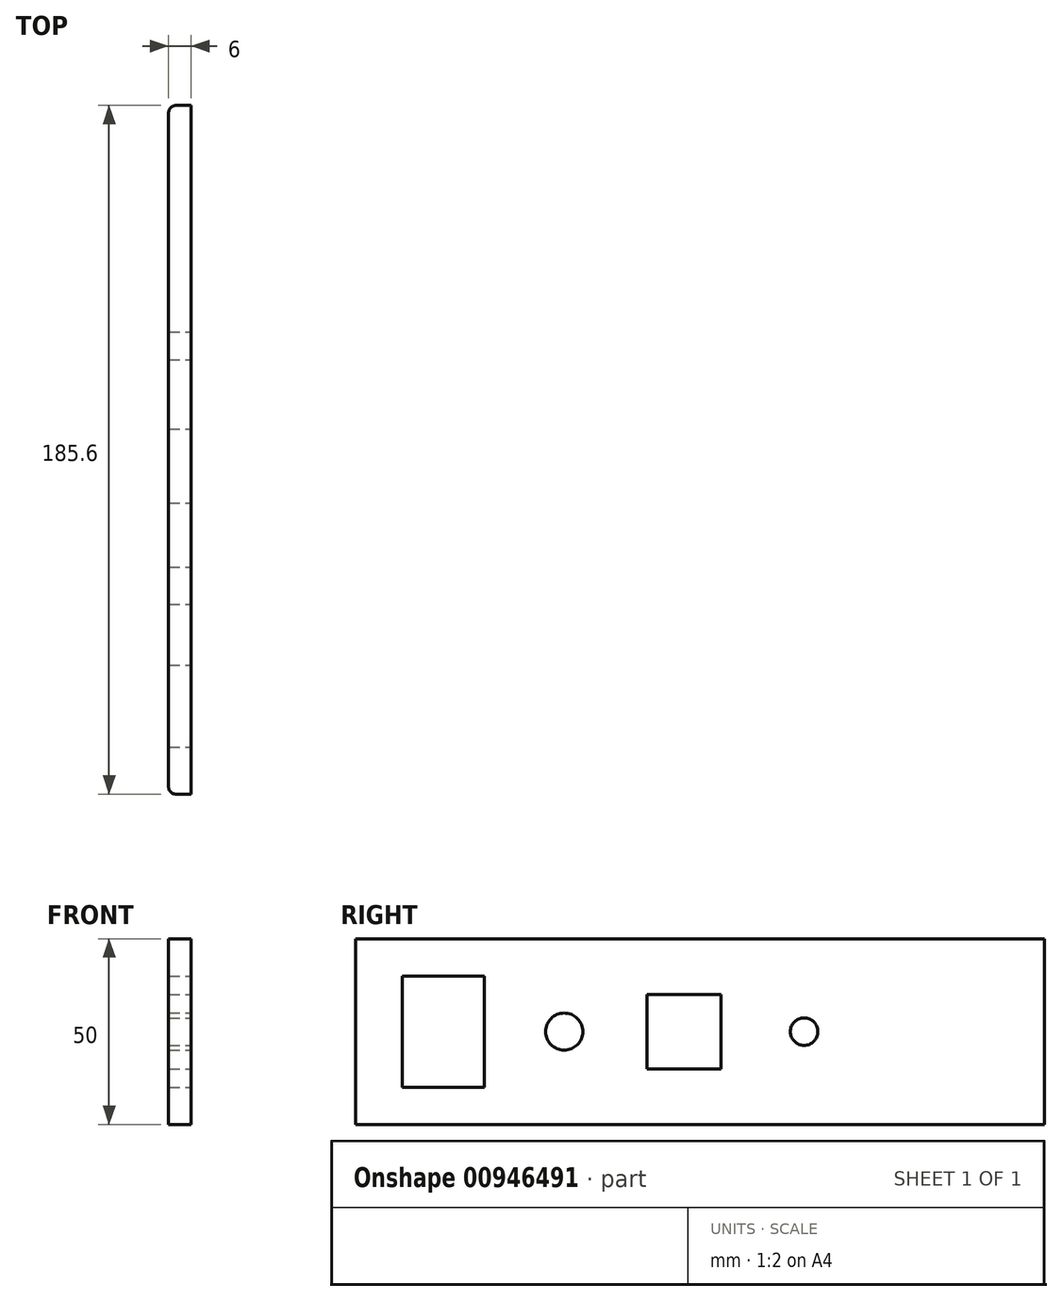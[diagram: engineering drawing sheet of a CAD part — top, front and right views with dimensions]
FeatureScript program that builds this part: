
annotation { "Feature Type Name" : "Feature", "Feature Type Description" : "" }
export const myFeature = defineFeature(function(context is Context, id is Id, definition is map)
    precondition{}
    {
        {
            var Q0;
            Q0=qCreatedBy(makeId("Right.planeOp"),FACE);
            var sketch = newSketch(context, id + "F0", { "sketchPlane" : qUnion([Q0])});
            skLineSegment(sketch, "E0.bottom", {"start": v(92.8, 25) * mm, "end": v(-92.8, 25) * mm});
            skLineSegment(sketch, "E0.top", {"start": v(92.8, -25) * mm, "end": v(-92.8, -25) * mm});
            skLineSegment(sketch, "E0.left", {"start": v(92.8, 25) * mm, "end": v(92.8, -25) * mm});
            skLineSegment(sketch, "E0.right", {"start": v(-92.8, 25) * mm, "end": v(-92.8, -25) * mm});
            skPoint(sketch, "E0.middle", {"position": v(0, 0) * mm});
            skSolve(sketch);
        }
        {
            var Q0;
            Q0=makeQuery(id+"F0.imprint","IMPRINT",FACE,{"disambiguationData":[TD([[makeQuery(id+"F0.imprint","IMPRINT",EDGE,{"derivedFrom":sQuery(id+"F0.wireOp",EDGE,"E0.bottom")}),1.0]])]});
            extrude(context, id + "F1", {"entities" : qUnion([Q0]), "depth" : 6 * mm, "offsetDistance" : 25 * mm});
        }
        {
            var Q0;
            Q0=makeQuery(id+"F1.opExtrude","CAP_FACE",FACE,{"disambiguationData":[OSD([sQuery(id+"F0.wireOp",EDGE,"E0.bottom"),sQuery(id+"F0.wireOp",EDGE,"E0.top"),sQuery(id+"F0.wireOp",EDGE,"E0.left"),sQuery(id+"F0.wireOp",EDGE,"E0.right")])],"isStart":false});
            var sketch = newSketch(context, id + "F2", { "sketchPlane" : qUnion([Q0])});
            skLineSegment(sketch, "E1.bottom", {"start": v(-58.05, -15) * mm, "end": v(-80.15, -15) * mm});
            skLineSegment(sketch, "E1.top", {"start": v(-58.05, 15) * mm, "end": v(-80.15, 15) * mm});
            skLineSegment(sketch, "E1.left", {"start": v(-58.05, -15) * mm, "end": v(-58.05, 15) * mm});
            skLineSegment(sketch, "E1.right", {"start": v(-80.15, -15) * mm, "end": v(-80.15, 15) * mm});
            skPoint(sketch, "E1.middle", {"position": v(-69.1, 0) * mm});
            skSolve(sketch);
        }
        {
            var Q0;
            Q0=makeQuery(id+"F2.imprint","IMPRINT",FACE,{"disambiguationData":[TD([[makeQuery(id+"F2.imprint","IMPRINT",EDGE,{"derivedFrom":sQuery(id+"F2.wireOp",EDGE,"E1.bottom")}),-1.0]])]});
            extrude(context, id + "F3", {"entities" : qUnion([Q0]), "operationType" : NewBodyOperationType.REMOVE, "endBound" : BoundingType.UP_TO_NEXT, "oppositeDirection" : true, "depth" : 25 * mm, "offsetDistance" : 25 * mm});
        }
        {
            var Q0;
            Q0=makeQuery(id+"F1.opExtrude","CAP_FACE",FACE,{"disambiguationData":[OSD([sQuery(id+"F0.wireOp",EDGE,"E0.bottom"),sQuery(id+"F0.wireOp",EDGE,"E0.top"),sQuery(id+"F0.wireOp",EDGE,"E0.left"),sQuery(id+"F0.wireOp",EDGE,"E0.right")])],"isStart":false});
            var sketch = newSketch(context, id + "F4", { "sketchPlane" : qUnion([Q0])});
            skCircle(sketch, "E2", {"center": v(-36.6, 0) * mm, "radius": 5 * mm});
            skSolve(sketch);
        }
        {
            var Q0;
            Q0=makeQuery(id+"F4.imprint","IMPRINT",FACE,{"disambiguationData":[TD([[makeQuery(id+"F4.imprint","IMPRINT",EDGE,{"derivedFrom":sQuery(id+"F4.wireOp",EDGE,"E2")}),1.0]])]});
            var Q1;
            Q1=sQuery(id+"F4.wireOp",EDGE,"E2");
            extrude(context, id + "F5", {"entities" : qUnion([Q0]), "operationType" : NewBodyOperationType.REMOVE, "surfaceEntities" : qUnion([Q1]), "endBound" : BoundingType.UP_TO_NEXT, "oppositeDirection" : true, "depth" : 25 * mm, "offsetDistance" : 25 * mm});
        }
        {
            var Q0;
            Q0=makeQuery(id+"F1.opExtrude","CAP_FACE",FACE,{"disambiguationData":[OSD([sQuery(id+"F0.wireOp",EDGE,"E0.bottom"),sQuery(id+"F0.wireOp",EDGE,"E0.top"),sQuery(id+"F0.wireOp",EDGE,"E0.left"),sQuery(id+"F0.wireOp",EDGE,"E0.right")])],"isStart":false});
            var sketch = newSketch(context, id + "F6", { "sketchPlane" : qUnion([Q0])});
            skLineSegment(sketch, "E3.bottom", {"start": v(5.65, -10) * mm, "end": v(-14.35, -10) * mm});
            skLineSegment(sketch, "E3.top", {"start": v(5.65, 10) * mm, "end": v(-14.35, 10) * mm});
            skLineSegment(sketch, "E3.left", {"start": v(5.65, -10) * mm, "end": v(5.65, 10) * mm});
            skLineSegment(sketch, "E3.right", {"start": v(-14.35, -10) * mm, "end": v(-14.35, 10) * mm});
            skPoint(sketch, "E3.middle", {"position": v(-4.35, 0) * mm});
            skSolve(sketch);
        }
        {
            var Q0;
            Q0=makeQuery(id+"F6.imprint","IMPRINT",FACE,{"disambiguationData":[TD([[makeQuery(id+"F6.imprint","IMPRINT",EDGE,{"derivedFrom":sQuery(id+"F6.wireOp",EDGE,"E3.bottom")}),-1.0]])]});
            extrude(context, id + "F7", {"entities" : qUnion([Q0]), "operationType" : NewBodyOperationType.REMOVE, "endBound" : BoundingType.UP_TO_NEXT, "oppositeDirection" : true, "depth" : 25 * mm, "offsetDistance" : 25 * mm});
        }
        {
            var Q0;
            Q0=makeQuery(id+"F1.opExtrude","CAP_FACE",FACE,{"disambiguationData":[OSD([sQuery(id+"F0.wireOp",EDGE,"E0.bottom"),sQuery(id+"F0.wireOp",EDGE,"E0.top"),sQuery(id+"F0.wireOp",EDGE,"E0.left"),sQuery(id+"F0.wireOp",EDGE,"E0.right")])],"isStart":false});
            var sketch = newSketch(context, id + "F8", { "sketchPlane" : qUnion([Q0])});
            skCircle(sketch, "E4", {"center": v(28.03, 0) * mm, "radius": 3.7 * mm});
            skSolve(sketch);
        }
        {
            var Q0;
            Q0=makeQuery(id+"F8.imprint","IMPRINT",FACE,{"disambiguationData":[TD([[makeQuery(id+"F8.imprint","IMPRINT",EDGE,{"derivedFrom":sQuery(id+"F8.wireOp",EDGE,"E4")}),1.0]])]});
            var Q1;
            Q1=sQuery(id+"F8.wireOp",EDGE,"E4");
            extrude(context, id + "F9", {"entities" : qUnion([Q0]), "operationType" : NewBodyOperationType.REMOVE, "surfaceEntities" : qUnion([Q1]), "endBound" : BoundingType.UP_TO_NEXT, "oppositeDirection" : true, "depth" : 25 * mm, "offsetDistance" : 25 * mm});
        }
        {
            var Q0;
            Q0=makeQuery(id+"F1.opExtrude","CAP_EDGE",EDGE,{"disambiguationData":[OSD([sQuery(id+"F0.wireOp",EDGE,"E0.left")])],"isStart":true});
            var Q1;
            Q1=makeQuery(id+"F1.opExtrude","CAP_EDGE",EDGE,{"disambiguationData":[OSD([sQuery(id+"F0.wireOp",EDGE,"E0.right")])],"isStart":true});
            fillet(context, id + "F10", {"entities" : qUnion([Q0, Q1]), "radius" : 2 * mm, "tangentPropagation" : true, "allowEdgeOverflow" : false});
        }
    });
